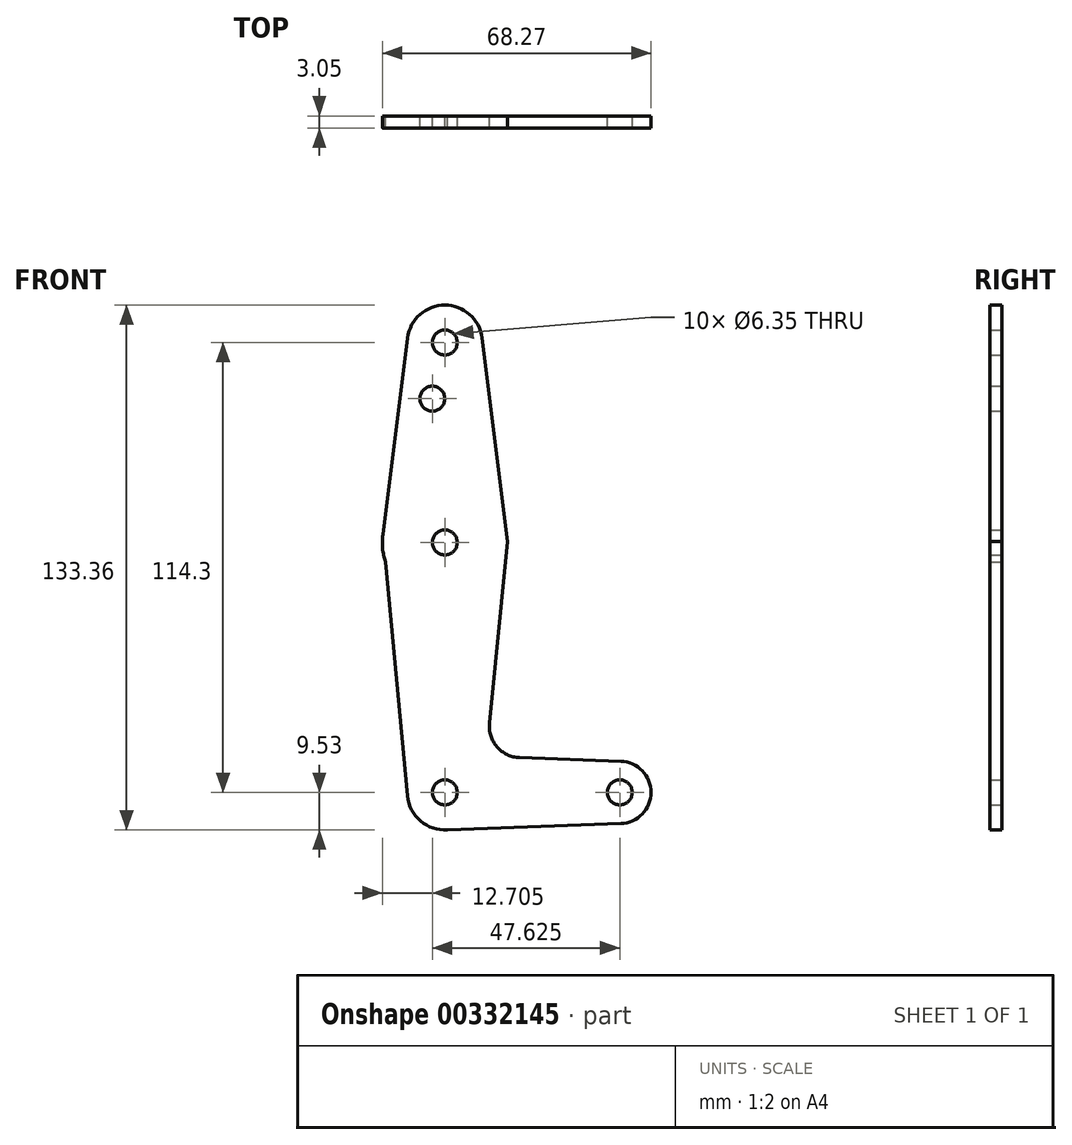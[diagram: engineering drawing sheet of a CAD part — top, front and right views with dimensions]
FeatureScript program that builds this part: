
annotation { "Feature Type Name" : "Feature", "Feature Type Description" : "" }
export const myFeature = defineFeature(function(context is Context, id is Id, definition is map)
    precondition{}
    {
        {
            var Q0;
            Q0=qCreatedBy(makeId("Front.planeOp"),FACE);
            var sketch = newSketch(context, id + "F0", { "sketchPlane" : qUnion([Q0])});
            skLineSegment(sketch, "E0", {"start": v(0, 0) * mm, "end": v(0, 63.5) * mm, "construction": true});
            skLineSegment(sketch, "E1", {"start": v(0, 0) * mm, "end": v(44.45, 0) * mm, "construction": true});
            skCircle(sketch, "E2", {"center": v(0, 63.5) * mm, "radius": 15.88 * mm});
            skCircle(sketch, "E3", {"center": v(0, 114.3) * mm, "radius": 9.53 * mm});
            skCircle(sketch, "E4", {"center": v(0, 0) * mm, "radius": 9.52 * mm});
            skCircle(sketch, "E5", {"center": v(44.45, 0) * mm, "radius": 7.94 * mm});
            skLineSegment(sketch, "E6", {"start": v(0, 114.3) * mm, "end": v(0, 63.5) * mm, "construction": true});
            skLineSegment(sketch, "E7", {"start": v(-9.45, 115.5) * mm, "end": v(-15.75, 65.48) * mm});
            skLineSegment(sketch, "E8", {"start": v(9.45, 115.5) * mm, "end": v(15.98, 63.7) * mm});
            skLineSegment(sketch, "E9", {"start": v(-15.75, 65.48) * mm, "end": v(-9.48, -0.9) * mm});
            skLineSegment(sketch, "E10", {"start": v(15.98, 63.7) * mm, "end": v(11.34, 17.59) * mm});
            skLineSegment(sketch, "E11", {"start": v(18.97, 8.85) * mm, "end": v(44.73, 7.93) * mm});
            skLineSegment(sketch, "E12", {"start": v(0, -9.52) * mm, "end": v(44.73, -7.93) * mm});
            skCircle(sketch, "E13", {"center": v(0, 114.3) * mm, "radius": 3.18 * mm});
            skCircle(sketch, "E14", {"center": v(0, 63.5) * mm, "radius": 3.18 * mm});
            skCircle(sketch, "E15", {"center": v(0, 0) * mm, "radius": 3.18 * mm});
            skCircle(sketch, "E16", {"center": v(44.45, 0) * mm, "radius": 3.18 * mm});
            skCircle(sketch, "E17", {"center": v(-3.18, 100.03) * mm, "radius": 3.18 * mm});
            skArc(sketch, "E18.filletArc", {"start": v(11.34, 17.59) * mm, "mid": v(13.26, 11.57) * mm, "end": v(18.97, 8.85) * mm});
            skSolve(sketch);
        }
        {
            var Q0;
            Q0 = qSketchRegion(id + "F0", true);
            extrude(context, id + "F1", {"entities" : qUnion([Q0]), "depth" : 3.05 * mm});
        }
        {
            var Q0;
            Q0 = qSketchRegion(id + "F0", true);
            extrude(context, id + "F2", {"entities" : qUnion([Q0]), "depth" : 3.05 * mm});
        }
    });
